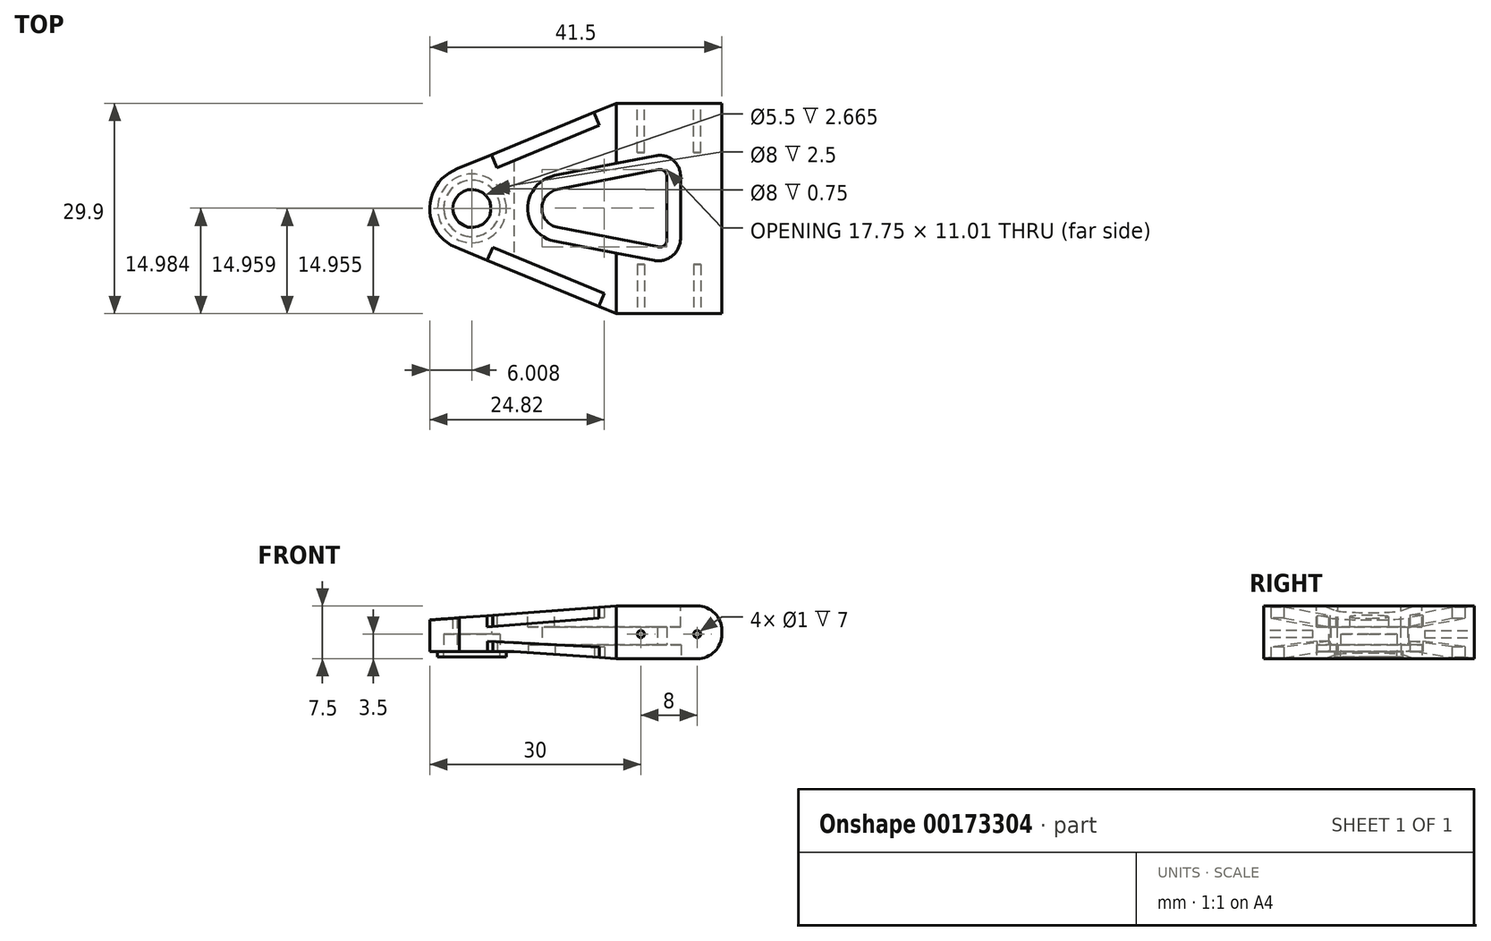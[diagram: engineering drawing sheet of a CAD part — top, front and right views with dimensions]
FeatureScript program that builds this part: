
annotation { "Feature Type Name" : "Feature", "Feature Type Description" : "" }
export const myFeature = defineFeature(function(context is Context, id is Id, definition is map)
    precondition{}
    {
        {
            var Q0;
            Q0=qCreatedBy(makeId("Top.planeOp"),FACE);
            var sketch = newSketch(context, id + "F0", { "sketchPlane" : qUnion([Q0])});
            skLineSegment(sketch, "E0", {"start": v(0, -14.95) * mm, "end": v(-14, -14.95) * mm});
            skLineSegment(sketch, "E1", {"start": v(-14, -14.95) * mm, "end": v(-36.28, -5.73) * mm});
            skLineSegment(sketch, "E2", {"start": v(-14, 14.95) * mm, "end": v(0, 14.95) * mm});
            skLineSegment(sketch, "E3", {"start": v(-36.58, 5.63) * mm, "end": v(-14, 14.95) * mm});
            skArc(sketch, "E4", {"start": v(-36.58, 5.63) * mm, "mid": v(-40.5, -0.15) * mm, "end": v(-36.28, -5.73) * mm});
            skLineSegment(sketch, "E5", {"start": v(1, -14.95) * mm, "end": v(1, 14.95) * mm});
            skLineSegment(sketch, "E6", {"start": v(0, -14.95) * mm, "end": v(1, -14.95) * mm});
            skLineSegment(sketch, "E7", {"start": v(0, 14.95) * mm, "end": v(1, 14.95) * mm});
            skSolve(sketch);
        }
        {
            var Q0;
            Q0=qCreatedBy(makeId("Top.planeOp"),FACE);
            var sketch = newSketch(context, id + "F1", { "sketchPlane" : qUnion([Q0])});
            skCircle(sketch, "E8", {"center": v(-34.5, 0) * mm, "radius": 2.75 * mm});
            skCircle(sketch, "E9", {"center": v(-34.5, 0) * mm, "radius": 4 * mm});
            skArc(sketch, "E10", {"start": v(-22.32, 2.7) * mm, "mid": v(-24.55, 0) * mm, "end": v(-22.32, -2.7) * mm});
            skLineSegment(sketch, "E11", {"start": v(-6.8, 4.5) * mm, "end": v(-6.8, -4.5) * mm});
            skArc(sketch, "E12", {"start": v(-6.8, 4.5) * mm, "mid": v(-7.16, 5.3) * mm, "end": v(-8, 5.52) * mm});
            skArc(sketch, "E13", {"start": v(-8.17, -5.4) * mm, "mid": v(-7.23, -5.3) * mm, "end": v(-6.8, -4.46) * mm});
            skLineSegment(sketch, "E14", {"start": v(-8.17, -5.4) * mm, "end": v(-22.32, -2.7) * mm});
            skLineSegment(sketch, "E15", {"start": v(-22.32, 2.7) * mm, "end": v(-8, 5.52) * mm});
            skSolve(sketch);
        }
        {
            var Q0;
            Q0 = qSketchRegion(id + "F0", true);
            extrude(context, id + "F2", {"entities" : qUnion([Q0]), "depth" : 7.5 * mm});
        }
        {
            var Q0;
            Q0=makeQuery(id+"F1.imprint","IMPRINT",FACE,{"disambiguationData":[TD([[makeQuery(id+"F1.imprint","IMPRINT",EDGE,{"derivedFrom":sQuery(id+"F1.wireOp",EDGE,"E10")}),1.0]])]});
            var Q1;
            Q1=makeQuery(id+"F1.imprint","IMPRINT",FACE,{"disambiguationData":[TD([[makeQuery(id+"F1.imprint","IMPRINT",EDGE,{"derivedFrom":sQuery(id+"F1.wireOp",EDGE,"E8")}),1.0]])]});
            extrude(context, id + "F3", {"entities" : qUnion([Q0, Q1]), "operationType" : NewBodyOperationType.REMOVE, "depth" : 25 * mm});
        }
        {
            var Q0;
            Q0=qCreatedBy(makeId("Front.planeOp"),FACE);
            var sketch = newSketch(context, id + "F4", { "sketchPlane" : qUnion([Q0])});
            skLineSegment(sketch, "E16", {"start": v(-40.52, 5.5) * mm, "end": v(-13.79, 7.51) * mm});
            skLineSegment(sketch, "E17", {"start": v(-13.79, 7.51) * mm, "end": v(-10.59, 12.88) * mm});
            skLineSegment(sketch, "E18", {"start": v(-10.59, 12.88) * mm, "end": v(-44.8, 12.16) * mm});
            skLineSegment(sketch, "E19", {"start": v(-44.8, 12.16) * mm, "end": v(-43.9, 0) * mm});
            skLineSegment(sketch, "E20", {"start": v(-43.9, 0) * mm, "end": v(-40.52, 0) * mm});
            skLineSegment(sketch, "E21", {"start": v(-40.52, 1) * mm, "end": v(-40.52, 0) * mm});
            skLineSegment(sketch, "E22", {"start": v(-40.52, 1) * mm, "end": v(-28.52, 1) * mm});
            skLineSegment(sketch, "E23", {"start": v(-28.52, 1) * mm, "end": v(-14, 0) * mm});
            skLineSegment(sketch, "E24", {"start": v(-14, 0) * mm, "end": v(-14.33, -1.73) * mm});
            skLineSegment(sketch, "E25", {"start": v(-14.33, -1.73) * mm, "end": v(-44.32, -1.73) * mm});
            skLineSegment(sketch, "E26", {"start": v(-44.32, -1.73) * mm, "end": v(-43.9, 0) * mm});
            skLineSegment(sketch, "E27", {"start": v(-40.52, 5.5) * mm, "end": v(-40.52, 1) * mm});
            skSolve(sketch);
        }
        {
            var Q0;
            Q0 = qSketchRegion(id + "F4", true);
            extrude(context, id + "F5", {"entities" : qUnion([Q0]), "operationType" : NewBodyOperationType.REMOVE, "endBound" : BoundingType.SYMMETRIC, "oppositeDirection" : true, "depth" : 30 * mm});
        }
        {
            var Q0;
            Q0 = qSketchRegion(id + "F1", true);
            var Q1;
            Q1=sQuery(id+"F1.wireOp",EDGE,"E9");
            extrude(context, id + "F6", {"entities" : qUnion([Q0]), "operationType" : NewBodyOperationType.REMOVE, "surfaceEntities" : qUnion([Q1]), "depth" : 3.5 * mm});
        }
        {
            var Q0;
            Q0=qCreatedBy(makeId("Top.planeOp"),FACE);
            var sketch = newSketch(context, id + "F7", { "sketchPlane" : qUnion([Q0])});
            skArc(sketch, "E28.0", {"start": v(-22.32, -2.7) * mm, "mid": v(-24.55, 0) * mm, "end": v(-22.32, 2.7) * mm});
            skLineSegment(sketch, "E28.1", {"start": v(-22.32, 2.7) * mm, "end": v(-22.32, 2.7) * mm});
            skLineSegment(sketch, "E28.2", {"start": v(-8, 5.52) * mm, "end": v(-13.98, 4.34) * mm});
            skArc(sketch, "E28.3", {"start": v(-8, 5.52) * mm, "mid": v(-7.16, 5.3) * mm, "end": v(-6.8, 4.5) * mm});
            skLineSegment(sketch, "E28.4", {"start": v(-6.8, -4.46) * mm, "end": v(-6.8, 4.5) * mm});
            skArc(sketch, "E28.5", {"start": v(-6.8, -4.46) * mm, "mid": v(-7.23, -5.3) * mm, "end": v(-8.17, -5.4) * mm});
            skLineSegment(sketch, "E28.6", {"start": v(-13.98, -4.3) * mm, "end": v(-8.17, -5.4) * mm});
            skLineSegment(sketch, "E28.7", {"start": v(-22.32, -2.7) * mm, "end": v(-22.32, -2.7) * mm});
            skLineSegment(sketch, "E29.0", {"start": v(-14.39, 6.3) * mm, "end": v(-22.67, 4.68) * mm});
            skLineSegment(sketch, "E30.0", {"start": v(-8.3, 7.5) * mm, "end": v(-14.39, 6.3) * mm});
            skLineSegment(sketch, "E31.0", {"start": v(-4.8, -4.38) * mm, "end": v(-4.8, 4.55) * mm});
            skLineSegment(sketch, "E32.0", {"start": v(-14.38, -6.25) * mm, "end": v(-8.55, -7.37) * mm});
            skLineSegment(sketch, "E33.0", {"start": v(-22.7, -4.66) * mm, "end": v(-14.38, -6.25) * mm});
            skArc(sketch, "E34", {"start": v(-22.67, 4.68) * mm, "mid": v(-26.52, 0.02) * mm, "end": v(-22.7, -4.66) * mm});
            skArc(sketch, "E35", {"start": v(-8.55, -7.37) * mm, "mid": v(-5.99, -6.74) * mm, "end": v(-4.8, -4.38) * mm});
            skArc(sketch, "E36", {"start": v(-4.8, 4.55) * mm, "mid": v(-5.84, 6.86) * mm, "end": v(-8.3, 7.5) * mm});
            skSolve(sketch);
        }
        {
            var Q0;
            Q0 = qSketchRegion(id + "F7", true);
            extrude(context, id + "F8", {"entities" : qUnion([Q0]), "operationType" : NewBodyOperationType.REMOVE, "depth" : 2 * mm});
        }
        {
            var Q0;
            Q0=makeQuery(id+"F2.opExtrude","CAP_FACE",FACE,{"disambiguationData":[OSD([sQuery(id+"F0.wireOp",EDGE,"um1QLLeK-tIpn-WBkH-jd5w-2k8M8m7FMOfL"),sQuery(id+"F0.wireOp",EDGE,"E0"),sQuery(id+"F0.wireOp",EDGE,"E1"),sQuery(id+"F0.wireOp",EDGE,"E2"),sQuery(id+"F0.wireOp",EDGE,"E3"),sQuery(id+"F0.wireOp",EDGE,"E4")])],"isStart":false});
            var sketch = newSketch(context, id + "F9", { "sketchPlane" : qUnion([Q0])});
            skLineSegment(sketch, "E37.0", {"start": v(-22.75, 4.67) * mm, "end": v(-25.77, 4.08) * mm});
            skLineSegment(sketch, "E38.0", {"start": v(-8.37, 7.5) * mm, "end": v(-25.77, 4.08) * mm});
            skLineSegment(sketch, "E39.0", {"start": v(-4.88, -4.39) * mm, "end": v(-4.88, 4.54) * mm});
            skLineSegment(sketch, "E40.0", {"start": v(-25.79, -4.09) * mm, "end": v(-8.62, -7.37) * mm});
            skLineSegment(sketch, "E41.0", {"start": v(-25.79, -4.09) * mm, "end": v(-22.77, -4.67) * mm});
            skArc(sketch, "E42", {"start": v(-22.75, 4.67) * mm, "mid": v(-26.59, 0.01) * mm, "end": v(-22.77, -4.67) * mm});
            skArc(sketch, "E43", {"start": v(-8.62, -7.37) * mm, "mid": v(-6.06, -6.74) * mm, "end": v(-4.88, -4.39) * mm});
            skArc(sketch, "E44", {"start": v(-4.88, 4.54) * mm, "mid": v(-5.91, 6.86) * mm, "end": v(-8.37, 7.5) * mm});
            skSolve(sketch);
        }
        {
            var Q0;
            Q0 = qSketchRegion(id + "F9", true);
            extrude(context, id + "F10", {"entities" : qUnion([Q0]), "operationType" : NewBodyOperationType.REMOVE, "oppositeDirection" : true, "depth" : 3 * mm});
        }
        {
            var Q0;
            Q0=makeQuery(id+"F5.boolean.opBoolean","COPY",FACE,{"derivedFrom":makeQuery(id+"F5.opExtrude","SWEPT_FACE",FACE,{"disambiguationData":[OSD([sQuery(id+"F4.wireOp",EDGE,"E22")])]})});
            var sketch = newSketch(context, id + "F11", { "sketchPlane" : qUnion([Q0])});
            skCircle(sketch, "E45", {"center": v(-34.5, 0) * mm, "radius": 4 * mm});
            skCircle(sketch, "E46", {"center": v(-34.5, 0) * mm, "radius": 4.88 * mm});
            skSolve(sketch);
        }
        {
            var Q0;
            Q0 = qSketchRegion(id + "F11", true);
            extrude(context, id + "F12", {"entities" : qUnion([Q0]), "operationType" : NewBodyOperationType.ADD, "depth" : 0.75 * mm});
        }
        {
            var Q0;
            Q0=makeQuery(id+"F2.opExtrude","SWEPT_FACE",FACE,{"disambiguationData":[OSD([sQuery(id+"F0.wireOp",EDGE,"E1")])]});
            var sketch = newSketch(context, id + "F13", { "sketchPlane" : qUnion([Q0])});
            skLineSegment(sketch, "E47", {"start": v(-27.04, 7.58) * mm, "end": v(-27.04, 4.5) * mm});
            skLineSegment(sketch, "E48", {"start": v(-9.87, 8.9) * mm, "end": v(-9.87, 5.81) * mm});
            skLineSegment(sketch, "E49", {"start": v(-27, 2.5) * mm, "end": v(-27, -0.5) * mm});
            skLineSegment(sketch, "E50", {"start": v(-9.83, 1.67) * mm, "end": v(-9.83, -1.33) * mm});
            skLineSegment(sketch, "E51", {"start": v(-27.04, 7.58) * mm, "end": v(-9.87, 8.9) * mm});
            skLineSegment(sketch, "E52", {"start": v(-9.87, 5.81) * mm, "end": v(-27.04, 4.5) * mm});
            skLineSegment(sketch, "E53", {"start": v(-27, 2.5) * mm, "end": v(-9.83, 1.67) * mm});
            skLineSegment(sketch, "E54", {"start": v(-9.83, -1.33) * mm, "end": v(-27, -0.5) * mm});
            skSolve(sketch);
        }
        {
            var Q0;
            Q0 = qSketchRegion(id + "F13", true);
            extrude(context, id + "F14", {"entities" : qUnion([Q0]), "operationType" : NewBodyOperationType.REMOVE, "oppositeDirection" : true, "depth" : 2 * mm});
        }
        {
            var Q0;
            Q0=makeQuery(id+"F2.opExtrude","SWEPT_FACE",FACE,{"disambiguationData":[OSD([sQuery(id+"F0.wireOp",EDGE,"E3")])]});
            var sketch = newSketch(context, id + "F15", { "sketchPlane" : qUnion([Q0])});
            skLineSegment(sketch, "E55.MirrorCS", {"start": v(26.37, 7.45) * mm, "end": v(26.37, 4.66) * mm});
            skLineSegment(sketch, "E56.MirrorCS", {"start": v(10.64, 8.58) * mm, "end": v(10.64, 5.76) * mm});
            skLineSegment(sketch, "E57.MirrorCS", {"start": v(26.31, 2.5) * mm, "end": v(26.32, -0.32) * mm});
            skLineSegment(sketch, "E58.MirrorCS", {"start": v(10.62, 1.72) * mm, "end": v(10.62, -1.03) * mm});
            skLineSegment(sketch, "E59", {"start": v(10.64, 8.58) * mm, "end": v(26.37, 7.45) * mm});
            skLineSegment(sketch, "E60", {"start": v(26.37, 4.66) * mm, "end": v(10.64, 5.76) * mm});
            skLineSegment(sketch, "E61", {"start": v(10.62, 1.72) * mm, "end": v(26.31, 2.5) * mm});
            skLineSegment(sketch, "E62", {"start": v(26.32, -0.32) * mm, "end": v(10.62, -1.03) * mm});
            skSolve(sketch);
        }
        {
            var Q0;
            Q0 = qSketchRegion(id + "F15", true);
            extrude(context, id + "F16", {"entities" : qUnion([Q0]), "operationType" : NewBodyOperationType.REMOVE, "oppositeDirection" : true, "depth" : 2 * mm});
        }
        {
            var Q0;
            Q0=makeQuery(id+"F2.opExtrude","SWEPT_FACE",FACE,{"disambiguationData":[OSD([sQuery(id+"F0.wireOp",EDGE,"E2")])]});
            var sketch = newSketch(context, id + "F17", { "sketchPlane" : qUnion([Q0])});
            skLineSegment(sketch, "E63", {"start": v(-5.7, 3.5) * mm, "end": v(19.62, 3.5) * mm, "construction": true});
            skLineSegment(sketch, "E64", {"start": v(2.5, 9.07) * mm, "end": v(2.5, -2.45) * mm, "construction": true});
            skLineSegment(sketch, "E65", {"start": v(10.5, 9.14) * mm, "end": v(10.5, -2.63) * mm, "construction": true});
            skCircle(sketch, "E66", {"center": v(2.5, 3.5) * mm, "radius": 0.5 * mm});
            skPoint(sketch, "E66.centerSnap0", {"position": v(2.5, 3.3) * mm});
            skCircle(sketch, "E67", {"center": v(10.5, 3.5) * mm, "radius": 0.5 * mm});
            skSolve(sketch);
        }
        {
            var Q0;
            Q0 = qSketchRegion(id + "F17", true);
            extrude(context, id + "F18", {"entities" : qUnion([Q0]), "operationType" : NewBodyOperationType.REMOVE, "oppositeDirection" : true, "depth" : 7 * mm});
        }
        {
            var Q0;
            Q0=makeQuery(id+"F2.opExtrude","SWEPT_FACE",FACE,{"disambiguationData":[OSD([sQuery(id+"F0.wireOp",EDGE,"E0"),sQuery(id+"F0.wireOp",EDGE,"E6")])]});
            var sketch = newSketch(context, id + "F19", { "sketchPlane" : qUnion([Q0])});
            skLineSegment(sketch, "E68", {"start": v(-2.5, 17.04) * mm, "end": v(-2.5, -9.23) * mm, "construction": true});
            skLineSegment(sketch, "E69", {"start": v(-10.5, 16.58) * mm, "end": v(-10.5, -6.7) * mm, "construction": true});
            skLineSegment(sketch, "E70", {"start": v(-15.2, 3.5) * mm, "end": v(3.92, 3.5) * mm, "construction": true});
            skCircle(sketch, "E71", {"center": v(-10.5, 3.5) * mm, "radius": 0.5 * mm});
            skCircle(sketch, "E72", {"center": v(-2.5, 3.5) * mm, "radius": 0.5 * mm});
            skPoint(sketch, "E72.centerSnap0", {"position": v(-2.5, 3.9) * mm});
            skSolve(sketch);
        }
        {
            var Q0;
            Q0 = qSketchRegion(id + "F19", true);
            extrude(context, id + "F20", {"entities" : qUnion([Q0]), "operationType" : NewBodyOperationType.REMOVE, "oppositeDirection" : true, "depth" : 7 * mm});
        }
        {
            var Q0;
            Q0=makeQuery(id+"F2.opExtrude","CAP_EDGE",EDGE,{"disambiguationData":[OSD([sQuery(id+"F0.wireOp",EDGE,"E5")])],"isStart":false});
            var Q1;
            Q1=makeQuery(id+"F2.opExtrude","CAP_EDGE",EDGE,{"disambiguationData":[OSD([sQuery(id+"F0.wireOp",EDGE,"E5")])],"isStart":true});
            fillet(context, id + "F21", {"entities" : qUnion([Q0, Q1]), "radius" : 3.5 * mm, "tangentPropagation" : true, "allowEdgeOverflow" : false});
        }
    });
